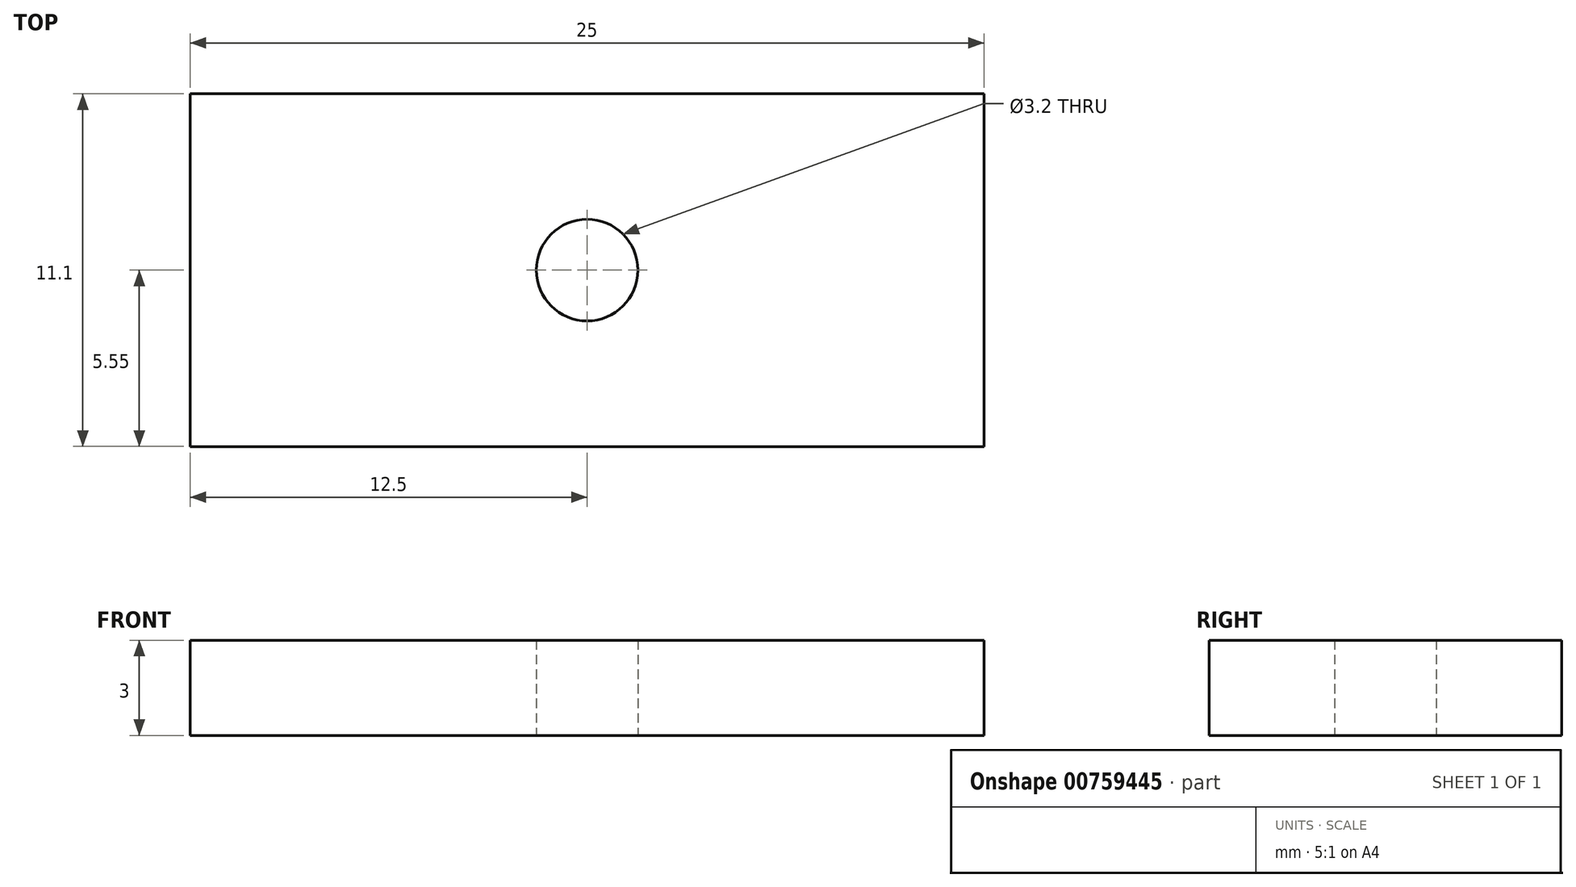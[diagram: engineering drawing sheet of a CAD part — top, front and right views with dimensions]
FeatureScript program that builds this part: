
annotation { "Feature Type Name" : "Feature", "Feature Type Description" : "" }
export const myFeature = defineFeature(function(context is Context, id is Id, definition is map)
    precondition{}
    {
        {
            var Q0;
            Q0=qCreatedBy(makeId("Top.planeOp"),FACE);
            var sketch = newSketch(context, id + "F0", { "sketchPlane" : qUnion([Q0])});
            skLineSegment(sketch, "E0.bottom", {"start": v(12.5, 5.55) * mm, "end": v(-12.5, 5.55) * mm});
            skLineSegment(sketch, "E0.top", {"start": v(12.5, -5.55) * mm, "end": v(-12.5, -5.55) * mm});
            skLineSegment(sketch, "E0.left", {"start": v(12.5, 5.55) * mm, "end": v(12.5, -5.55) * mm});
            skLineSegment(sketch, "E0.right", {"start": v(-12.5, 5.55) * mm, "end": v(-12.5, -5.55) * mm});
            skPoint(sketch, "E0.middle", {"position": v(0, 0) * mm});
            skCircle(sketch, "E1", {"center": v(0, 0) * mm, "radius": 1.6 * mm});
            skSolve(sketch);
        }
        {
            var Q0;
            Q0=makeQuery(id+"F0.imprint","IMPRINT",FACE,{"disambiguationData":[TD([[makeQuery(id+"F0.imprint","IMPRINT",EDGE,{"derivedFrom":sQuery(id+"F0.wireOp",EDGE,"E0.bottom")}),1.0]])]});
            extrude(context, id + "F1", {"entities" : qUnion([Q0]), "depth" : 3 * mm, "offsetDistance" : 25 * mm});
        }
    });
